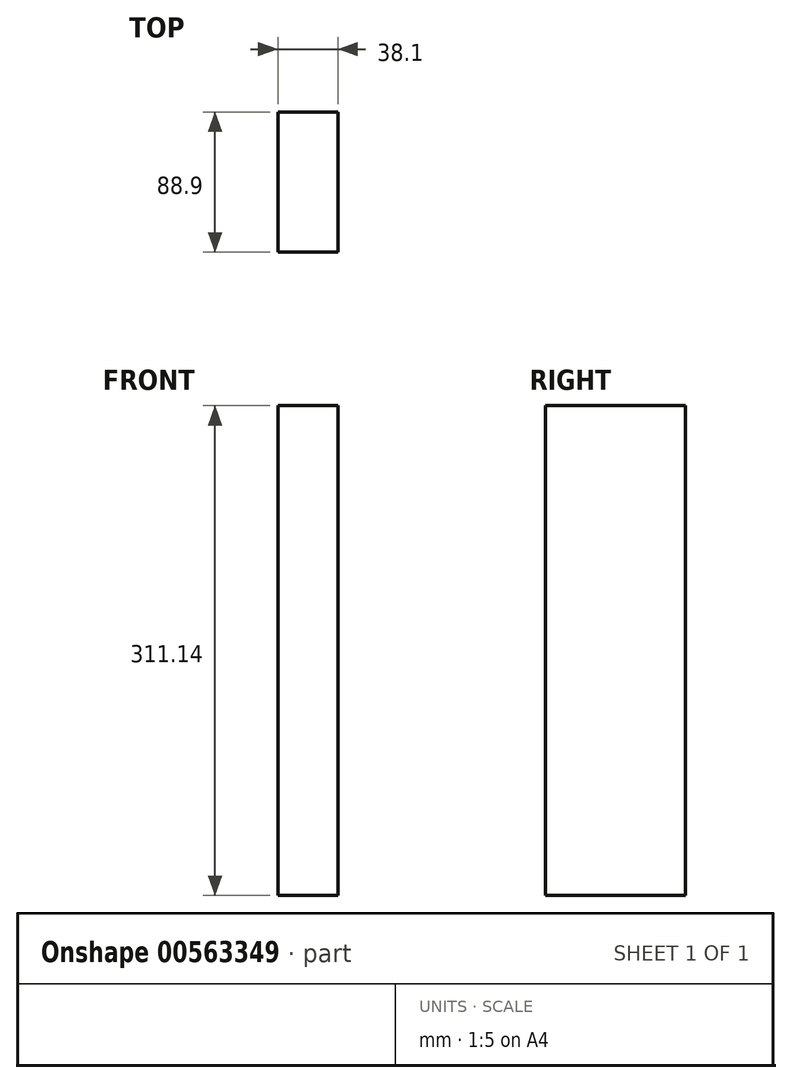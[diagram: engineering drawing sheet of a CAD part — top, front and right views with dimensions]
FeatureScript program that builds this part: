
annotation { "Feature Type Name" : "Feature", "Feature Type Description" : "" }
export const myFeature = defineFeature(function(context is Context, id is Id, definition is map)
    precondition{}
    {
        {
            var Q0;
            Q0=qCreatedBy(makeId("Front.planeOp"),FACE);
            var sketch = newSketch(context, id + "F0", { "sketchPlane" : qUnion([Q0])});
            skLineSegment(sketch, "E0.bottom", {"start": v(19.05, -155.58) * mm, "end": v(-19.05, -155.58) * mm});
            skLineSegment(sketch, "E0.top", {"start": v(19.05, 155.58) * mm, "end": v(-19.05, 155.58) * mm});
            skLineSegment(sketch, "E0.left", {"start": v(19.05, -155.58) * mm, "end": v(19.05, 155.58) * mm});
            skLineSegment(sketch, "E0.right", {"start": v(-19.05, -155.58) * mm, "end": v(-19.05, 155.58) * mm});
            skPoint(sketch, "E0.middle", {"position": v(0, 0) * mm});
            skSolve(sketch);
        }
        {
            var Q0;
            Q0 = qSketchRegion(id + "F0", true);
            extrude(context, id + "F1", {"entities" : qUnion([Q0]), "depth" : 88.9 * mm, "offsetDistance" : 25.4 * mm});
        }
    });
